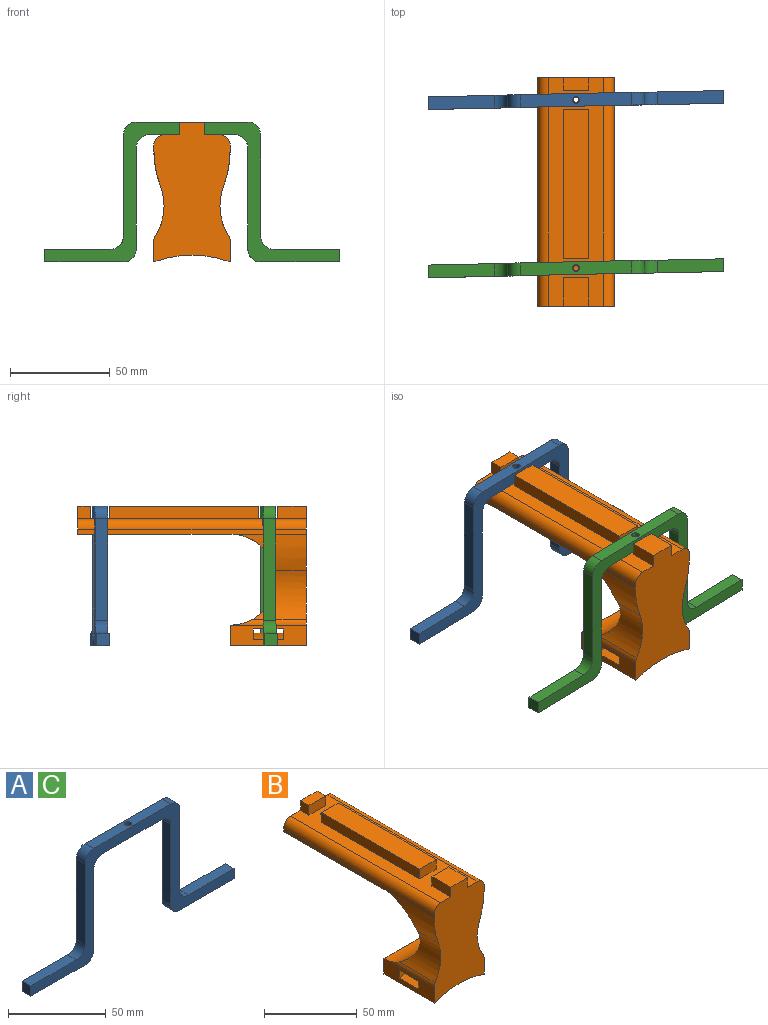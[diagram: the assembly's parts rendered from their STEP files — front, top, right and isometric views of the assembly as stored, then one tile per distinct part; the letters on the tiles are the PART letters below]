
ASSEMBLY  parts=3 mates=3
PART A: 23 faces, bbox 147.3x6.4x69.9 mm
  f0: plane 43.18x6.35mm, normal (0,0,-1), area 264.3mm2, adj f1,f19,f20,f21,f22
  f1: cylinder r=6.35mm len=6.35mm, axis (0,1,0), area 63.3mm2, adj f0,f2,f20,f21
  f2: plane 50.8x6.35mm, normal (-1,0,0), area 322.6mm2, adj f1,f3,f20,f21
  f3: cylinder r=6.35mm len=6.35mm, axis (0,1,0), area 63.3mm2, adj f2,f4,f20,f21
  f4: plane 39.37x6.35mm, normal (0,0,-1), area 250mm2, adj f3,f5,f20,f21
  f5: plane 6.35x6.35mm, normal (1,0,0), area 40.3mm2, adj f4,f6,f20,f21
  f6: plane 33.02x6.35mm, normal (0,0,1), area 209.7mm2, adj f5,f7,f20,f21
  f7: cylinder r=6.35mm len=6.35mm, axis (0,1,0), area 63.3mm2, adj f6,f8,f20,f21
  f8: plane 50.8x6.35mm, normal (1,0,0), area 322.6mm2, adj f7,f9,f20,f21
  f9: cylinder r=6.35mm len=6.35mm, axis (0,1,0), area 63.3mm2, adj f8,f10,f20,f21
  f10: plane 55.88x6.35mm, normal (0,0,1), area 344.9mm2, adj f9,f11,f20,f21,f22
  f11: cylinder r=6.35mm len=6.35mm, axis (0,1,0), area 63.3mm2, adj f10,f12,f20,f21
  f12: plane 50.8x6.35mm, normal (-1,0,0), area 322.6mm2, adj f11,f13,f20,f21
  f13: cylinder r=6.35mm len=6.35mm, axis (0,1,0), area 63.3mm2, adj f12,f14,f20,f21
  f14: plane 33.02x6.35mm, normal (0,0,1), area 209.7mm2, adj f13,f15,f20,f21
  f15: plane 6.35x6.35mm, normal (-1,0,0), area 40.3mm2, adj f14,f16,f20,f21
  f16: plane 39.37x6.35mm, normal (0,0,-1), area 250mm2, adj f15,f17,f20,f21
  f17: cylinder r=6.35mm len=6.35mm, axis (0,1,0), area 63.3mm2, adj f16,f18,f20,f21
  f18: plane 50.8x6.35mm, normal (1,0,0), area 322.6mm2, adj f17,f19,f20,f21
  f19: cylinder r=6.35mm len=6.35mm, axis (0,1,0), area 63.3mm2, adj f0,f18,f20,f21
  f20: plane 147.32x69.85mm, normal (0,-1,0), area 1741.9mm2, adj f0,f1,f2,f3,f4,f5,f6,f7
  f21: plane 147.32x69.85mm, normal (0,1,0), area 1741.9mm2, adj f0,f1,f2,f3,f4,f5,f6,f7
  f22: cylinder r=1.78mm len=6.35mm, axis (0,0,1), area 70.9mm2, adj f0,f10
PART B: 39 faces, bbox 38.1x114.3x69.9 mm
  f0: plane 38.1x10.34mm, normal (1,0,0), area 315.2mm2, adj f2,f3,f10,f11,f12,f13,f14,f34
  f1: plane 38.1x10.34mm, normal (-1,0,0), area 315.2mm2, adj f2,f3,f10,f11,f12,f13,f14,f35
  f2: plane 38.1x10.34mm, normal (0,1,0), area 309.3mm2, adj f0,f1,f10,f36
  f3: plane 69.85x38.1mm, normal (0,-1,0), area 2165.5mm2, adj f0,f1,f7,f8,f9,f10,f22,f23
  f4: plane 6.35x6.35mm, normal (-1,0,0), area 40.3mm2, adj f6,f7,f26,f28
  f5: plane 74.61x6.35mm, normal (1,0,0), area 473.8mm2, adj f7,f18,f20,f27
  f6: plane 12.7x6.35mm, normal (0,0,1), area 80.6mm2, adj f4,f19,f26,f28
  f7: plane 114.3x27.94mm, normal (0,0,1), area 1971.6mm2, adj f3,f4,f5,f15,f17,f18,f19,f21
  f8: plane 114.3x2.66mm, normal (1,0,0), area 294.6mm2, adj f3,f25,f26,f32,f36,f37
  f9: plane 114.3x2.66mm, normal (-1,0,0), area 294.6mm2, adj f3,f25,f26,f33,f36,f38
  f10: cylinder r=56.37mm len=38.1mm, axis (0,1,0), area 1480.8mm2, adj f0,f1,f2,f3
  f11: cylinder r=64.37mm len=38.1mm, axis (0,-1,0), area 580.2mm2, adj f0,f1,f13,f14
  f12: cylinder r=59.37mm len=38.1mm, axis (0,-1,0), area 581.8mm2, adj f0,f1,f13,f14
  f13: plane 38.1x8.14mm, normal (0,-1,0), area 193.7mm2, adj f0,f1,f11,f12
  f14: plane 38.1x8.14mm, normal (0,1,0), area 193.7mm2, adj f0,f1,f11,f12
  f15: cylinder r=1.4mm len=12.7mm, axis (0,0,1), area 111.5mm2, adj f7,f16
  f16: plane 2.79x2.79mm, normal (0,0,1), area 6.1mm2, adj f15
  f17: plane 74.61x6.35mm, normal (-1,0,0), area 473.8mm2, adj f7,f18,f20,f27
  f18: plane 12.7x6.35mm, normal (0,-1,0), area 80.6mm2, adj f5,f7,f17,f20
  f19: plane 6.35x6.35mm, normal (1,0,0), area 40.3mm2, adj f6,f7,f26,f28
  f20: plane 74.61x12.7mm, normal (0,0,1), area 947.6mm2, adj f5,f17,f18,f27
  f21: plane 12.7x6.35mm, normal (0,1,0), area 80.6mm2, adj f7,f22,f23,f24
  f22: plane 14.29x6.35mm, normal (-1,0,0), area 90.7mm2, adj f3,f7,f21,f24
  f23: plane 14.29x6.35mm, normal (1,0,0), area 90.7mm2, adj f3,f7,f21,f24
  f24: plane 14.29x12.7mm, normal (0,0,1), area 181.5mm2, adj f3,f21,f22,f23
  f25: plane 76.2x38.1mm, normal (0,0,-1), area 2897.1mm2, adj f8,f9,f26,f29,f36
  f26: plane 38.1x13.97mm, normal (0,1,0), area 359.9mm2, adj f4,f6,f7,f8,f9,f19,f25,f37
  f27: plane 12.7x6.35mm, normal (0,1,0), area 80.6mm2, adj f5,f7,f17,f20
  f28: plane 12.7x6.35mm, normal (0,-1,0), area 80.6mm2, adj f4,f6,f7,f19
  f29: cylinder r=1.4mm len=7.62mm, axis (0,0,1), area 66.9mm2, adj f7,f25
  f30: cylinder r=27.94mm len=27.33mm, axis (0,1,0), area 471.8mm2, adj f3,f33,f35,f36
  f31: cylinder r=27.94mm len=27.33mm, axis (0,1,0), area 471.8mm2, adj f3,f32,f34,f36
  f32: cylinder r=50.8mm len=35.81mm, axis (0,1,0), area 390.2mm2, adj f3,f8,f31,f36
  f33: cylinder r=50.8mm len=35.81mm, axis (0,1,0), area 390.2mm2, adj f3,f9,f30,f36
  f34: cylinder r=5.08mm len=38.1mm, axis (0,1,0), area 87.7mm2, adj f0,f3,f31,f36
  f35: cylinder r=5.08mm len=38.1mm, axis (0,1,0), area 87.7mm2, adj f1,f3,f30,f36
  f36: cylinder r=22.77mm len=45.54mm, axis (1,0,0), area 2456mm2, adj f2,f8,f9,f25,f30,f31,f32,f33
  f37: cylinder r=5.08mm len=114.3mm, axis (0,-1,0), area 912.1mm2, adj f3,f7,f8,f26
  f38: cylinder r=5.08mm len=114.3mm, axis (0,1,0), area 912.1mm2, adj f3,f7,f9,f26
PART C: same geometry as A
PLACE A rot(axis=(0,0,1),1.2deg) t=(-28.85,122.5,127.62)mm
PLACE B t=(-28.78,35.19,11.07)mm fixed
PLACE C rot(axis=(0,0,1),1.2deg) t=(-28.85,38.37,127.62)mm
MATE parallel A.f20 <-> C.f21  axis (0.02,-1,0) through (-0.78,116.75,95.87)mm
MATE revolute B.f29 <-> A.f22  axis (0,0,1) through (-28.78,119.33,127.62)mm
MATE revolute B.f15 <-> C.f22  axis (0,0,1) through (-28.78,35.19,127.62)mm
